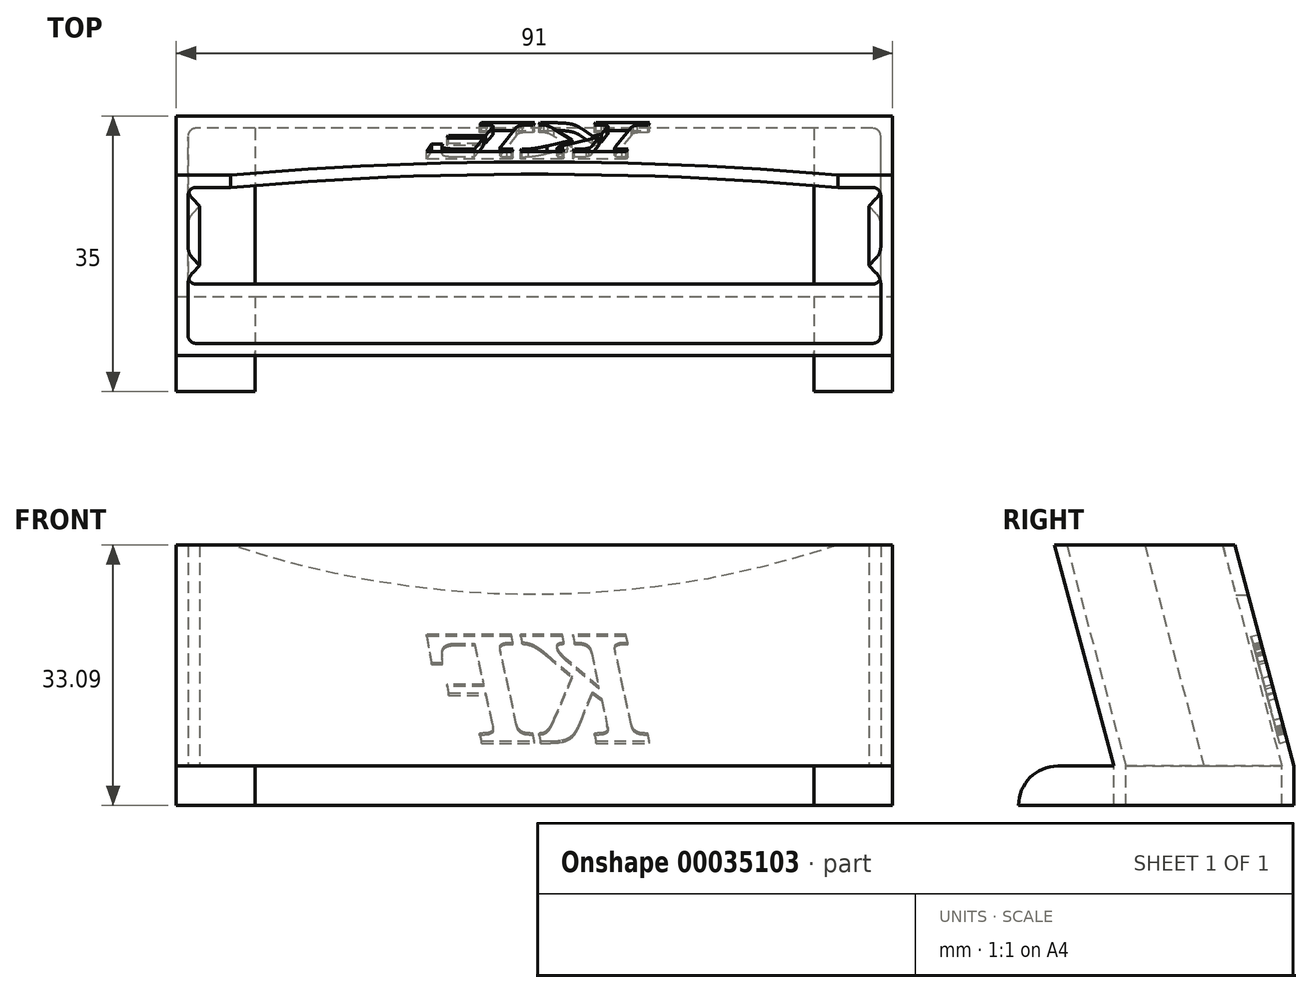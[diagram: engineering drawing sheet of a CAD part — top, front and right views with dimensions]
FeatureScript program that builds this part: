
annotation { "Feature Type Name" : "Feature", "Feature Type Description" : "" }
export const myFeature = defineFeature(function(context is Context, id is Id, definition is map)
    precondition{}
    {
        {
            var Q0;
            Q0=qCreatedBy(makeId("Top.planeOp"),FACE);
            var sketch = newSketch(context, id + "F0", { "sketchPlane" : qUnion([Q0])});
            skLineSegment(sketch, "E0", {"start": v(0, 0) * mm, "end": v(-43, 0) * mm});
            skLineSegment(sketch, "E1", {"start": v(-44, -1) * mm, "end": v(-44, -7.23) * mm});
            skLineSegment(sketch, "E2", {"start": v(-43.41, -8.64) * mm, "end": v(-42.5, -9.56) * mm});
            skLineSegment(sketch, "E3", {"start": v(-42.5, -9.56) * mm, "end": v(-45.5, -9.56) * mm});
            skLineSegment(sketch, "E4", {"start": v(-45.5, -9.56) * mm, "end": v(-45.5, 1.5) * mm});
            skLineSegment(sketch, "E5", {"start": v(-45.5, 1.5) * mm, "end": v(0, 1.5) * mm});
            skLineSegment(sketch, "E6", {"start": v(0, 1.5) * mm, "end": v(0, 0) * mm});
            skLineSegment(sketch, "E7", {"start": v(-45.5, -4.48) * mm, "end": v(-44, -4.48) * mm, "construction": true});
            skPoint(sketch, "E8.visualSharp", {"position": v(-44, 0) * mm});
            skArc(sketch, "E8.filletArc", {"start": v(-43, 0) * mm, "mid": v(-43.7, -0.3) * mm, "end": v(-44, -1) * mm});
            skPoint(sketch, "E9.visualSharp", {"position": v(-44, -8.06) * mm});
            skArc(sketch, "E9.filletArc", {"start": v(-44, -7.23) * mm, "mid": v(-43.85, -8) * mm, "end": v(-43.41, -8.64) * mm});
            skSolve(sketch);
        }
        {
            var Q0;
            Q0=makeQuery(id+"F0.imprint","IMPRINT",FACE,{"disambiguationData":[TD([[makeQuery(id+"F0.imprint","IMPRINT",EDGE,{"derivedFrom":sQuery(id+"F0.wireOp",EDGE,"E0")}),-1.0]])]});
            extrude(context, id + "F1", {"entities" : qUnion([Q0]), "depth" : 20 * mm});
        }
        {
            var Q0;
            Q0=makeQuery(id+"F1.opExtrude","SWEPT_BODY",BODY,{"disambiguationData":[OSD([sQuery(id+"F0.wireOp",EDGE,"E0"),sQuery(id+"F0.wireOp",EDGE,"E1"),sQuery(id+"F0.wireOp",EDGE,"E2"),sQuery(id+"F0.wireOp",EDGE,"E3"),sQuery(id+"F0.wireOp",EDGE,"E4"),sQuery(id+"F0.wireOp",EDGE,"E5"),sQuery(id+"F0.wireOp",EDGE,"E6"),sQuery(id+"F0.wireOp",EDGE,"E8.filletArc"),sQuery(id+"F0.wireOp",EDGE,"E9.filletArc")])]});
            var Q1;
            Q1=makeQuery(id+"F1.opExtrude","SWEPT_FACE",FACE,{"disambiguationData":[OSD([sQuery(id+"F0.wireOp",EDGE,"E3")])]});
            mirror(context, id + "F2", {"entities" : qUnion([Q0]), "mirrorPlane" : qUnion([Q1])});
        }
        {
            var Q0;
            Q0=makeQuery(id+"F1.opExtrude","SWEPT_BODY",BODY,{"disambiguationData":[OSD([sQuery(id+"F0.wireOp",EDGE,"E0"),sQuery(id+"F0.wireOp",EDGE,"E1"),sQuery(id+"F0.wireOp",EDGE,"E2"),sQuery(id+"F0.wireOp",EDGE,"E3"),sQuery(id+"F0.wireOp",EDGE,"E4"),sQuery(id+"F0.wireOp",EDGE,"E5"),sQuery(id+"F0.wireOp",EDGE,"E6"),sQuery(id+"F0.wireOp",EDGE,"E8.filletArc"),sQuery(id+"F0.wireOp",EDGE,"E9.filletArc")])]});
            var Q1;
            Q1=makeQuery(id+"F2.opPattern","COPY",BODY,{"derivedFrom":makeQuery(id+"F1.opExtrude","SWEPT_BODY",BODY,{"disambiguationData":[OSD([sQuery(id+"F0.wireOp",EDGE,"E0"),sQuery(id+"F0.wireOp",EDGE,"E1"),sQuery(id+"F0.wireOp",EDGE,"E2"),sQuery(id+"F0.wireOp",EDGE,"E3"),sQuery(id+"F0.wireOp",EDGE,"E4"),sQuery(id+"F0.wireOp",EDGE,"E5"),sQuery(id+"F0.wireOp",EDGE,"E6"),sQuery(id+"F0.wireOp",EDGE,"E8.filletArc"),sQuery(id+"F0.wireOp",EDGE,"E9.filletArc")])]}),"instanceName":"1"});
            var Q2;
            Q2=makeQuery(id+"F1.opExtrude","SWEPT_FACE",FACE,{"disambiguationData":[OSD([sQuery(id+"F0.wireOp",EDGE,"E6")])]});
            mirror(context, id + "F3", {"entities" : qUnion([Q0, Q1]), "mirrorPlane" : qUnion([Q2])});
        }
        {
            var Q0;
            Q0=makeQuery(id+"F1.opExtrude","SWEPT_BODY",BODY,{"disambiguationData":[OSD([sQuery(id+"F0.wireOp",EDGE,"E0"),sQuery(id+"F0.wireOp",EDGE,"E1"),sQuery(id+"F0.wireOp",EDGE,"E2"),sQuery(id+"F0.wireOp",EDGE,"E3"),sQuery(id+"F0.wireOp",EDGE,"E4"),sQuery(id+"F0.wireOp",EDGE,"E5"),sQuery(id+"F0.wireOp",EDGE,"E6"),sQuery(id+"F0.wireOp",EDGE,"E8.filletArc"),sQuery(id+"F0.wireOp",EDGE,"E9.filletArc")])]});
            var Q1;
            Q1=makeQuery(id+"F2.opPattern","COPY",BODY,{"derivedFrom":makeQuery(id+"F1.opExtrude","SWEPT_BODY",BODY,{"disambiguationData":[OSD([sQuery(id+"F0.wireOp",EDGE,"E0"),sQuery(id+"F0.wireOp",EDGE,"E1"),sQuery(id+"F0.wireOp",EDGE,"E2"),sQuery(id+"F0.wireOp",EDGE,"E3"),sQuery(id+"F0.wireOp",EDGE,"E4"),sQuery(id+"F0.wireOp",EDGE,"E5"),sQuery(id+"F0.wireOp",EDGE,"E6"),sQuery(id+"F0.wireOp",EDGE,"E8.filletArc"),sQuery(id+"F0.wireOp",EDGE,"E9.filletArc")])]}),"instanceName":"1"});
            var Q2;
            Q2=makeQuery(id+"F3.opPattern","COPY",BODY,{"derivedFrom":makeQuery(id+"F1.opExtrude","SWEPT_BODY",BODY,{"disambiguationData":[OSD([sQuery(id+"F0.wireOp",EDGE,"E0"),sQuery(id+"F0.wireOp",EDGE,"E1"),sQuery(id+"F0.wireOp",EDGE,"E2"),sQuery(id+"F0.wireOp",EDGE,"E3"),sQuery(id+"F0.wireOp",EDGE,"E4"),sQuery(id+"F0.wireOp",EDGE,"E5"),sQuery(id+"F0.wireOp",EDGE,"E6"),sQuery(id+"F0.wireOp",EDGE,"E8.filletArc"),sQuery(id+"F0.wireOp",EDGE,"E9.filletArc")])]}),"instanceName":"1"});
            var Q3;
            Q3=makeQuery(id+"F3.opPattern","COPY",BODY,{"derivedFrom":makeQuery(id+"F2.opPattern","COPY",BODY,{"derivedFrom":makeQuery(id+"F1.opExtrude","SWEPT_BODY",BODY,{"disambiguationData":[OSD([sQuery(id+"F0.wireOp",EDGE,"E0"),sQuery(id+"F0.wireOp",EDGE,"E1"),sQuery(id+"F0.wireOp",EDGE,"E2"),sQuery(id+"F0.wireOp",EDGE,"E3"),sQuery(id+"F0.wireOp",EDGE,"E4"),sQuery(id+"F0.wireOp",EDGE,"E5"),sQuery(id+"F0.wireOp",EDGE,"E6"),sQuery(id+"F0.wireOp",EDGE,"E8.filletArc"),sQuery(id+"F0.wireOp",EDGE,"E9.filletArc")])]}),"instanceName":"1"}),"instanceName":"1"});
            booleanBodies(context, id + "F4", {"operationType" : BooleanOperationType.UNION, "tools" : qUnion([Q0, Q1, Q2, Q3])});
        }
        {
            var Q0;
            {var subQ0=makeQuery(id+"F1.opExtrude","CAP_FACE",FACE,{"disambiguationData":[OSD([sQuery(id+"F0.wireOp",EDGE,"E0"),sQuery(id+"F0.wireOp",EDGE,"E1"),sQuery(id+"F0.wireOp",EDGE,"E2"),sQuery(id+"F0.wireOp",EDGE,"E3"),sQuery(id+"F0.wireOp",EDGE,"E4"),sQuery(id+"F0.wireOp",EDGE,"E5"),sQuery(id+"F0.wireOp",EDGE,"E6"),sQuery(id+"F0.wireOp",EDGE,"E8.filletArc"),sQuery(id+"F0.wireOp",EDGE,"E9.filletArc")])],"isStart":false});var subQ1=makeQuery(id+"F2.opPattern","COPY",FACE,{"derivedFrom":subQ0,"instanceName":"1"});Q0=makeQuery(id+"F4.opBoolean","MERGE",FACE,{"derivedFrom":[subQ0,subQ1,makeQuery(id+"F3.opPattern","COPY",FACE,{"derivedFrom":subQ0,"instanceName":"1"}),makeQuery(id+"F3.opPattern","COPY",FACE,{"derivedFrom":subQ1,"instanceName":"1"})]});}
            extrude(context, id + "F5", {"entities" : qUnion([Q0]), "operationType" : NewBodyOperationType.ADD, "depth" : 15 * mm});
        }
        {
            var Q0;
            Q0=makeQuery(id+"F1.opExtrude","SWEPT_BODY",BODY,{"disambiguationData":[OSD([sQuery(id+"F0.wireOp",EDGE,"E0"),sQuery(id+"F0.wireOp",EDGE,"E1"),sQuery(id+"F0.wireOp",EDGE,"E2"),sQuery(id+"F0.wireOp",EDGE,"E3"),sQuery(id+"F0.wireOp",EDGE,"E4"),sQuery(id+"F0.wireOp",EDGE,"E5"),sQuery(id+"F0.wireOp",EDGE,"E6"),sQuery(id+"F0.wireOp",EDGE,"E8.filletArc"),sQuery(id+"F0.wireOp",EDGE,"E9.filletArc")])]});
            var Q1;
            {var subQ0=makeQuery(id+"F2.opPattern","COPY",EDGE,{"derivedFrom":makeQuery(id+"F1.opExtrude","CAP_EDGE",EDGE,{"disambiguationData":[OSD([sQuery(id+"F0.wireOp",EDGE,"E5")])],"isStart":true}),"instanceName":"1"});Q1=makeQuery(id+"F4.opBoolean","MERGE",EDGE,{"derivedFrom":[subQ0,makeQuery(id+"F3.opPattern","COPY",EDGE,{"derivedFrom":subQ0,"instanceName":"1"})]});}
            transform(context, id + "F6", {"entities" : qUnion([Q0]), "transformType" : TransformType.ROTATION, "transformAxis" : qUnion([Q1]), "angle" : 15 * degree, "makeCopy" : false});
        }
        {
            var Q0;
            {var subQ0=sQuery(id+"F0.wireOp",EDGE,"E4");var subQ1=makeQuery(id+"F1.opExtrude","SWEPT_FACE",FACE,{"disambiguationData":[OSD([subQ0])]});var subQ2=makeQuery(id+"F1.opExtrude","CAP_EDGE",EDGE,{"disambiguationData":[OSD([subQ0])],"isStart":false});Q0=makeQuery(id+"F5.boolean.opBoolean","MERGE",FACE,{"derivedFrom":[makeQuery(id+"F4.opBoolean","MERGE",FACE,{"derivedFrom":[makeQuery(id+"F3.opPattern","COPY",FACE,{"derivedFrom":subQ1,"instanceName":"1"}),makeQuery(id+"F3.opPattern","COPY",FACE,{"derivedFrom":makeQuery(id+"F2.opPattern","COPY",FACE,{"derivedFrom":subQ1,"instanceName":"1"}),"instanceName":"1"})]}),makeQuery(id+"F5.opExtrude","SWEPT_FACE",FACE,{"disambiguationData":[OSD([subQ0]),TDD([makeQuery(id+"F4.opBoolean","MERGE",EDGE,{"derivedFrom":[makeQuery(id+"F3.opPattern","COPY",EDGE,{"derivedFrom":subQ2,"instanceName":"1"}),makeQuery(id+"F3.opPattern","COPY",EDGE,{"derivedFrom":makeQuery(id+"F2.opPattern","COPY",EDGE,{"derivedFrom":subQ2,"instanceName":"1"}),"instanceName":"1"})]})])]})]});}
            var sketch = newSketch(context, id + "F7", { "sketchPlane" : qUnion([Q0])});
            skLineSegment(sketch, "E10", {"start": v(0.75, 5.72) * mm, "end": v(-22.15, 5.72) * mm});
            skLineSegment(sketch, "E11", {"start": v(-29.68, 33.8) * mm, "end": v(-6.78, 33.8) * mm});
            skSolve(sketch);
        }
        {
            var Q0;
            {var subQ3=sQuery(id+"F7.wireOp",EDGE,"E11");Q0=makeQuery(id+"F7.imprint","IMPRINT",FACE,{"disambiguationData":[TD([[makeQuery(id+"F7.imprint","IMPRINT",EDGE,{"derivedFrom":subQ3}),1.0]])]});}
            var Q1;
            {var subQ3=sQuery(id+"F7.wireOp",EDGE,"E10");Q1=makeQuery(id+"F7.imprint","IMPRINT",FACE,{"disambiguationData":[TD([[makeQuery(id+"F7.imprint","IMPRINT",EDGE,{"derivedFrom":subQ3}),1.0]])]});}
            extrude(context, id + "F8", {"entities" : qUnion([Q0, Q1]), "operationType" : NewBodyOperationType.REMOVE, "endBound" : BoundingType.THROUGH_ALL, "oppositeDirection" : true, "depth" : 25 * mm});
        }
        {
            var Q0;
            Q0=makeQuery(id+"F8.boolean.opBoolean","COPY",FACE,{"derivedFrom":makeQuery(id+"F8.opExtrude","SWEPT_FACE",FACE,{"disambiguationData":[OSD([sQuery(id+"F7.wireOp",EDGE,"E10")])]})});
            var sketch = newSketch(context, id + "F9", { "sketchPlane" : qUnion([Q0])});
            skLineSegment(sketch, "E12.bottom", {"start": v(45.5, -0.75) * mm, "end": v(35.5, -0.75) * mm});
            skLineSegment(sketch, "E12.top", {"start": v(45.5, 34.25) * mm, "end": v(35.5, 34.25) * mm});
            skLineSegment(sketch, "E12.left", {"start": v(45.5, -0.75) * mm, "end": v(45.5, 34.25) * mm});
            skLineSegment(sketch, "E12.right", {"start": v(35.5, -0.75) * mm, "end": v(35.5, 34.25) * mm});
            skLineSegment(sketch, "E13.bottom", {"start": v(-45.5, -0.75) * mm, "end": v(-35.5, -0.75) * mm});
            skLineSegment(sketch, "E13.top", {"start": v(-45.5, 34.25) * mm, "end": v(-35.5, 34.25) * mm});
            skLineSegment(sketch, "E13.left", {"start": v(-45.5, -0.75) * mm, "end": v(-45.5, 34.25) * mm});
            skLineSegment(sketch, "E13.right", {"start": v(-35.5, -0.75) * mm, "end": v(-35.5, 34.25) * mm});
            skSolve(sketch);
        }
        {
            var Q0;
            {var subQ8=sQuery(id+"F9.wireOp",EDGE,"E12.top");Q0=makeQuery(id+"F9.imprint","IMPRINT",FACE,{"disambiguationData":[TD([[makeQuery(id+"F9.imprint","IMPRINT",EDGE,{"derivedFrom":subQ8}),1.0]])]});}
            var Q1;
            {var subQ36=sQuery(id+"F9.wireOp",EDGE,"E12.bottom");Q1=makeQuery(id+"F9.imprint","IMPRINT",FACE,{"disambiguationData":[TD([[makeQuery(id+"F9.imprint","IMPRINT",EDGE,{"derivedFrom":subQ36}),1.0]])]});}
            var Q2;
            {var subQ3=makeQuery(id+"F8.opExtrude","SWEPT_FACE",FACE,{"disambiguationData":[OSD([sQuery(id+"F7.wireOp",EDGE,"E10")])]});var subQ18=sQuery(id+"F0.wireOp",EDGE,"E1");var subQ19=makeQuery(id+"F1.opExtrude","SWEPT_FACE",FACE,{"disambiguationData":[OSD([subQ18])]});var subQ20=makeQuery(id+"F1.opExtrude","CAP_EDGE",EDGE,{"disambiguationData":[OSD([subQ18])],"isStart":false});Q2=makeQuery(id+"F9.imprint","IMPRINT",FACE,{"disambiguationData":[TD([[makeQuery(id+"F9.imprint","IMPRINT",EDGE,{"derivedFrom":makeQuery(id+"F8.boolean.opBoolean","INTERSECT",EDGE,{"derivedFrom":[makeQuery(id+"F5.boolean.opBoolean","MERGE",FACE,{"derivedFrom":[makeQuery(id+"F3.opPattern","COPY",FACE,{"derivedFrom":subQ19,"instanceName":"1"}),makeQuery(id+"F5.opExtrude","SWEPT_FACE",FACE,{"disambiguationData":[OSD([subQ18]),TDD([makeQuery(id+"F3.opPattern","COPY",EDGE,{"derivedFrom":subQ20,"instanceName":"1"})])]})]}),subQ3]})}),-1.0]])]});}
            var Q3;
            {var subQ8=sQuery(id+"F9.wireOp",EDGE,"E13.top");Q3=makeQuery(id+"F9.imprint","IMPRINT",FACE,{"disambiguationData":[TD([[makeQuery(id+"F9.imprint","IMPRINT",EDGE,{"derivedFrom":subQ8}),-1.0]])]});}
            var Q4;
            {var subQ36=sQuery(id+"F9.wireOp",EDGE,"E13.bottom");Q4=makeQuery(id+"F9.imprint","IMPRINT",FACE,{"disambiguationData":[TD([[makeQuery(id+"F9.imprint","IMPRINT",EDGE,{"derivedFrom":subQ36}),1.0]])]});}
            var Q5;
            {var subQ3=makeQuery(id+"F8.opExtrude","SWEPT_FACE",FACE,{"disambiguationData":[OSD([sQuery(id+"F7.wireOp",EDGE,"E10")])]});var subQ22=sQuery(id+"F0.wireOp",EDGE,"E1");var subQ23=makeQuery(id+"F1.opExtrude","SWEPT_FACE",FACE,{"disambiguationData":[OSD([subQ22])]});var subQ24=makeQuery(id+"F1.opExtrude","CAP_EDGE",EDGE,{"disambiguationData":[OSD([subQ22])],"isStart":false});Q5=makeQuery(id+"F9.imprint","IMPRINT",FACE,{"disambiguationData":[TD([[makeQuery(id+"F9.imprint","IMPRINT",EDGE,{"derivedFrom":makeQuery(id+"F8.boolean.opBoolean","INTERSECT",EDGE,{"derivedFrom":[makeQuery(id+"F5.boolean.opBoolean","MERGE",FACE,{"derivedFrom":[subQ23,makeQuery(id+"F5.opExtrude","SWEPT_FACE",FACE,{"disambiguationData":[OSD([subQ22]),TDD([subQ24])]})]}),subQ3]})}),-1.0]])]});}
            extrude(context, id + "F10", {"entities" : qUnion([Q0, Q1, Q2, Q3, Q4, Q5]), "operationType" : NewBodyOperationType.ADD, "depth" : 5 * mm});
        }
        {
            var Q0;
            Q0=makeQuery(id+"F10.opExtrude","CAP_EDGE",EDGE,{"disambiguationData":[OSD([sQuery(id+"F9.wireOp",EDGE,"E13.top")])],"isStart":true});
            var Q1;
            Q1=makeQuery(id+"F10.opExtrude","CAP_EDGE",EDGE,{"disambiguationData":[OSD([sQuery(id+"F9.wireOp",EDGE,"E12.top")])],"isStart":true});
            fillet(context, id + "F11", {"entities" : qUnion([Q0, Q1]), "radius" : 5 * mm, "tangentPropagation" : true, "allowEdgeOverflow" : false});
        }
        {
            var Q0;
            {var subQ6=sQuery(id+"F0.wireOp",EDGE,"E0");var subQ9=makeQuery(id+"F1.opExtrude","SWEPT_FACE",FACE,{"disambiguationData":[OSD([subQ6])]});Q0=makeQuery(id+"F10.boolean.opBoolean","SPLIT",FACE,{"disambiguationData":[TD([subQ9])],"derivedFrom":makeQuery(id+"F8.boolean.opBoolean","COPY",FACE,{"derivedFrom":makeQuery(id+"F8.opExtrude","SWEPT_FACE",FACE,{"disambiguationData":[OSD([sQuery(id+"F7.wireOp",EDGE,"E10")])]})})});}
            var Q1;
            {var subQ4=sQuery(id+"F0.wireOp",EDGE,"E0");var subQ7=makeQuery(id+"F2.opPattern","COPY",FACE,{"derivedFrom":makeQuery(id+"F1.opExtrude","SWEPT_FACE",FACE,{"disambiguationData":[OSD([subQ4])]}),"instanceName":"1"});Q1=makeQuery(id+"F10.boolean.opBoolean","SPLIT",FACE,{"disambiguationData":[TD([subQ7])],"derivedFrom":makeQuery(id+"F8.boolean.opBoolean","COPY",FACE,{"derivedFrom":makeQuery(id+"F8.opExtrude","SWEPT_FACE",FACE,{"disambiguationData":[OSD([sQuery(id+"F7.wireOp",EDGE,"E10")])]})})});}
            extrude(context, id + "F12", {"entities" : qUnion([Q0, Q1]), "operationType" : NewBodyOperationType.ADD, "depth" : 5 * mm});
        }
        {
            var Q0;
            Q0=qCreatedBy(makeId("Front.planeOp"),FACE);
            var sketch = newSketch(context, id + "F13", { "sketchPlane" : qUnion([Q0])});
            skLineSegment(sketch, "E14", {"start": v(0, 34.3) * mm, "end": v(-40, 34.3) * mm});
            skLineSegment(sketch, "E15", {"start": v(0, 34.3) * mm, "end": v(40, 34.3) * mm});
            skArc(sketch, "E16", {"start": v(-40, 34.3) * mm, "mid": v(0, 27.5) * mm, "end": v(40, 34.3) * mm});
            skSolve(sketch);
        }
        {
            var Q0;
            Q0=makeQuery(id+"F13.imprint","IMPRINT",FACE,{"disambiguationData":[TD([[makeQuery(id+"F13.imprint","IMPRINT",EDGE,{"derivedFrom":sQuery(id+"F13.wireOp",EDGE,"E14")}),1.0]])]});
            extrude(context, id + "F14", {"entities" : qUnion([Q0]), "operationType" : NewBodyOperationType.REMOVE, "depth" : 15 * mm});
        }
        {
            var Q0;
            {var subQ0=sQuery(id+"F0.wireOp",EDGE,"E5");var subQ1=makeQuery(id+"F1.opExtrude","SWEPT_FACE",FACE,{"disambiguationData":[OSD([subQ0])]});var subQ2=makeQuery(id+"F1.opExtrude","CAP_EDGE",EDGE,{"disambiguationData":[OSD([subQ0])],"isStart":false});Q0=makeQuery(id+"F5.boolean.opBoolean","MERGE",FACE,{"derivedFrom":[makeQuery(id+"F4.opBoolean","MERGE",FACE,{"derivedFrom":[subQ1,makeQuery(id+"F3.opPattern","COPY",FACE,{"derivedFrom":subQ1,"instanceName":"1"})]}),makeQuery(id+"F5.opExtrude","SWEPT_FACE",FACE,{"disambiguationData":[OSD([subQ0]),TDD([makeQuery(id+"F4.opBoolean","MERGE",EDGE,{"derivedFrom":[subQ2,makeQuery(id+"F3.opPattern","COPY",EDGE,{"derivedFrom":subQ2,"instanceName":"1"})]})])]})]});}
            var sketch = newSketch(context, id + "F15", { "sketchPlane" : qUnion([Q0])});
            skText(sketch, "E17", { "text": "KF", "fontName": "NotoSerif-BoldItalic.ttf"});
            const initialGuessF15  = {"E17": [-0.01417, 0.00862, 1, 0, 0.01416]};
            skSetInitialGuess(sketch, initialGuessF15);
            skSolve(sketch);
        }
        {
            var Q0;
            Q0=makeQuery(id+"F15.imprint","IMPRINT",FACE,{"disambiguationData":[TD([[makeQuery(id+"F15.imprint","IMPRINT",EDGE,{"derivedFrom":sQuery(id+"F15.wireOp",EDGE,"E17.sketch_text.stroke-0")}),-1.0]])]});
            var Q1;
            Q1=makeQuery(id+"F15.imprint","IMPRINT",FACE,{"disambiguationData":[TD([[makeQuery(id+"F15.imprint","IMPRINT",EDGE,{"derivedFrom":sQuery(id+"F15.wireOp",EDGE,"E17.sketch_text.stroke-61")}),-1.0]])]});
            extrude(context, id + "F16", {"entities" : qUnion([Q0, Q1]), "operationType" : NewBodyOperationType.REMOVE, "oppositeDirection" : true, "depth" : 1 * mm});
        }
    });
